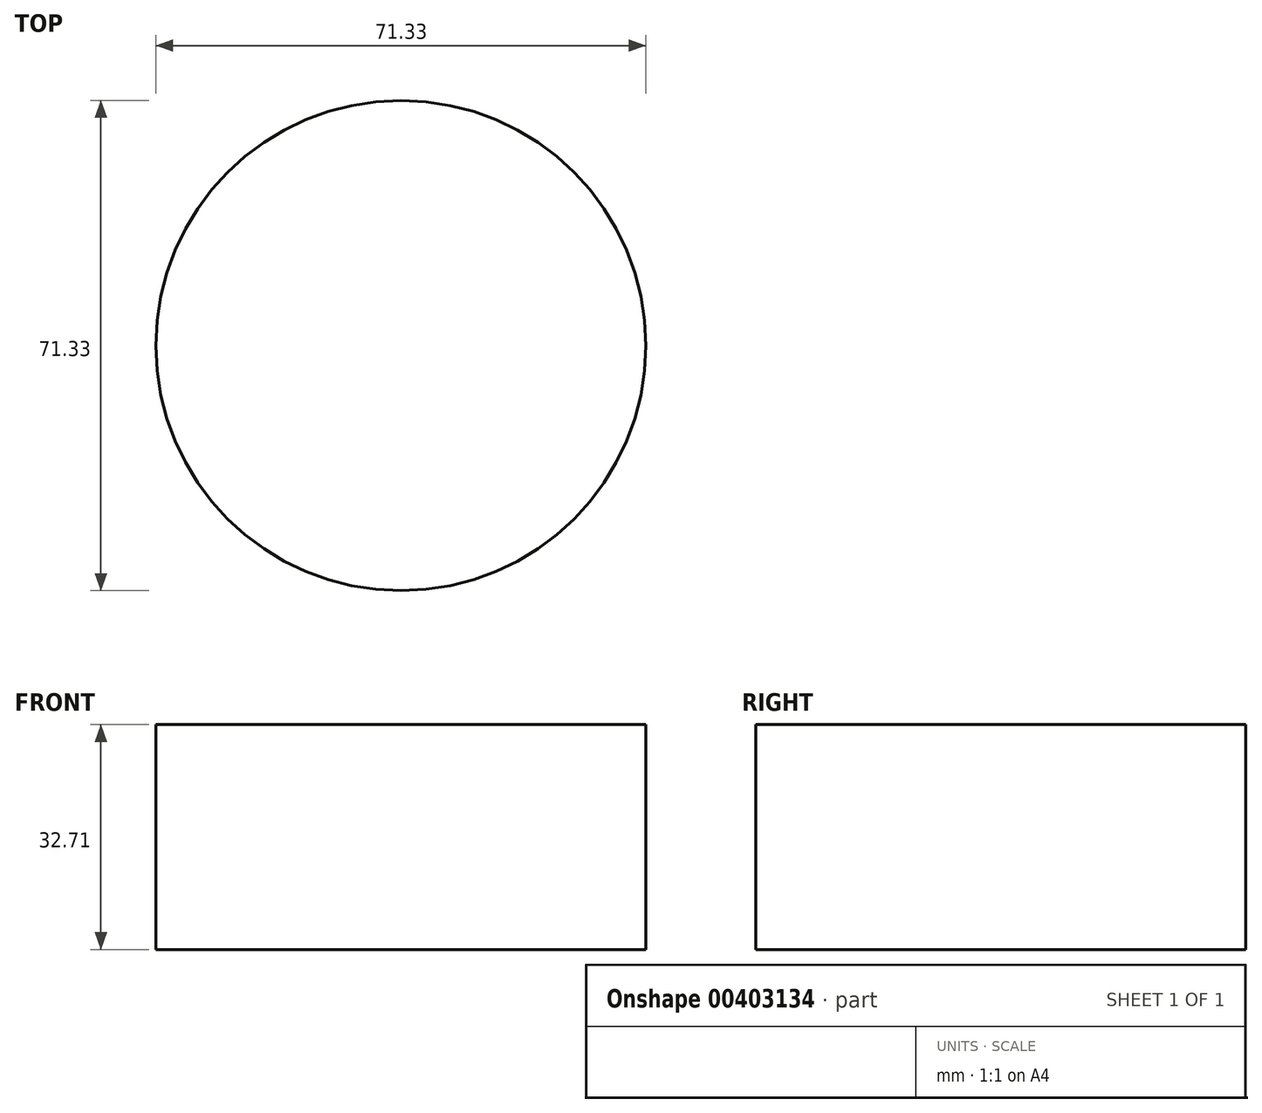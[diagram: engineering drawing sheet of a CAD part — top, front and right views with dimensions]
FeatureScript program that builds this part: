
annotation { "Feature Type Name" : "Feature", "Feature Type Description" : "" }
export const myFeature = defineFeature(function(context is Context, id is Id, definition is map)
    precondition{}
    {
        {
            var Q0;
            Q0=qCreatedBy(makeId("Top.planeOp"),FACE);
            var sketch = newSketch(context, id + "F0", { "sketchPlane" : qUnion([Q0])});
            skCircle(sketch, "E0", {"center": v(-4.78, 35.34) * mm, "radius": 35.66 * mm});
            skPoint(sketch, "E0.first.point", {"position": v(0, 0) * mm});
            skPoint(sketch, "E0.second.point", {"position": v(-40.32, 32.38) * mm});
            skPoint(sketch, "E0.third.point", {"position": v(30.02, 27.52) * mm});
            skSolve(sketch);
        }
        {
            var Q0;
            Q0 = qSketchRegion(id + "F0", true);
            var Q1;
            Q1=sQuery(id+"F0.wireOp",EDGE,"E0");
            extrude(context, id + "F1", {"entities" : qUnion([Q0]), "bodyType" : ToolBodyType.SURFACE, "surfaceEntities" : qUnion([Q1]), "depth" : 32.7 * mm});
        }
    });
